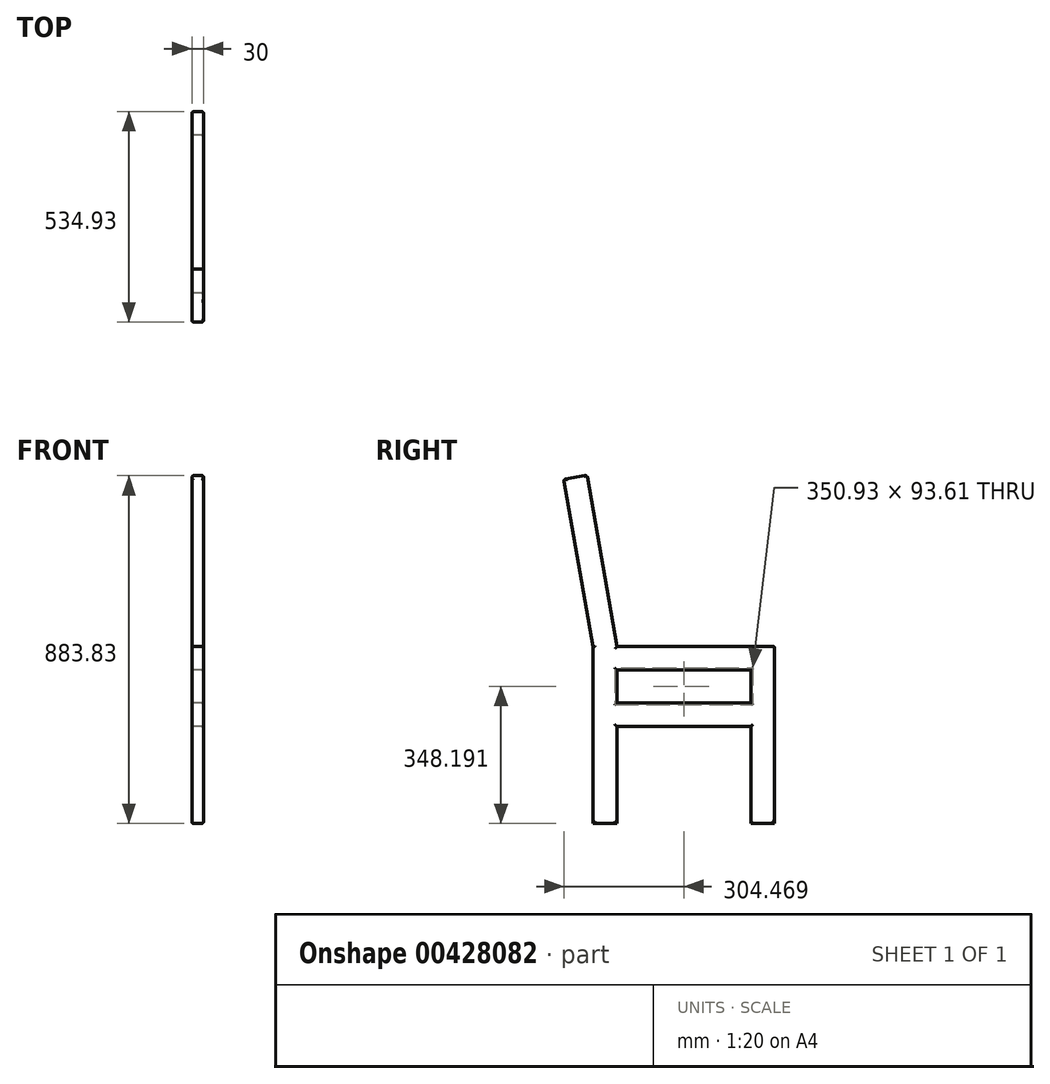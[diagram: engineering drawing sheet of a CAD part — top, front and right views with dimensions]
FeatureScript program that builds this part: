
annotation { "Feature Type Name" : "Feature", "Feature Type Description" : "" }
export const myFeature = defineFeature(function(context is Context, id is Id, definition is map)
    precondition{}
    {
        {
            var Q0;
            Q0=qCreatedBy(makeId("Right.planeOp"),FACE);
            var sketch = newSketch(context, id + "F0", { "sketchPlane" : qUnion([Q0])});
            skLineSegment(sketch, "E0", {"start": v(-254.48, -181.61) * mm, "end": v(-254.48, 268.39) * mm});
            skLineSegment(sketch, "E1", {"start": v(-254.48, 268.39) * mm, "end": v(-329.28, 692.6) * mm});
            skLineSegment(sketch, "E2", {"start": v(-329.28, 692.6) * mm, "end": v(-270.2, 703.02) * mm});
            skLineSegment(sketch, "E3", {"start": v(-270.2, 703.02) * mm, "end": v(-193.56, 268.39) * mm});
            skLineSegment(sketch, "E4", {"start": v(-193.56, 268.39) * mm, "end": v(206.44, 268.39) * mm});
            skLineSegment(sketch, "E5", {"start": v(206.44, 268.39) * mm, "end": v(206.44, -181.61) * mm});
            skLineSegment(sketch, "E6", {"start": v(206.44, -181.61) * mm, "end": v(146.44, -181.61) * mm});
            skLineSegment(sketch, "E7", {"start": v(146.44, -181.61) * mm, "end": v(146.44, 208.39) * mm});
            skLineSegment(sketch, "E8", {"start": v(146.44, 208.39) * mm, "end": v(-194.48, 208.39) * mm});
            skLineSegment(sketch, "E9", {"start": v(-194.48, 208.39) * mm, "end": v(-194.48, -181.61) * mm});
            skLineSegment(sketch, "E10", {"start": v(-194.48, -181.61) * mm, "end": v(-254.48, -181.61) * mm});
            skLineSegment(sketch, "E11", {"start": v(-194.48, 124.78) * mm, "end": v(146.44, 124.78) * mm});
            skLineSegment(sketch, "E12", {"start": v(-194.48, 64.78) * mm, "end": v(146.44, 64.78) * mm});
            skSolve(sketch);
        }
        {
            var Q0;
            Q0 = qSketchRegion(id + "F0", true);
            extrude(context, id + "F1", {"entities" : qUnion([Q0]), "depth" : 30 * mm});
        }
        {
            var Q0;
            Q0=makeQuery(id+"F1.opExtrude","CAP_FACE",FACE,{"disambiguationData":[OSD([sQuery(id+"F0.wireOp",EDGE,"E0"),sQuery(id+"F0.wireOp",EDGE,"E1"),sQuery(id+"F0.wireOp",EDGE,"E2"),sQuery(id+"F0.wireOp",EDGE,"E3"),sQuery(id+"F0.wireOp",EDGE,"E4"),sQuery(id+"F0.wireOp",EDGE,"E5"),sQuery(id+"F0.wireOp",EDGE,"E6"),sQuery(id+"F0.wireOp",EDGE,"E7"),sQuery(id+"F0.wireOp",EDGE,"E8"),sQuery(id+"F0.wireOp",EDGE,"E9"),sQuery(id+"F0.wireOp",EDGE,"E10")])],"isStart":false});
            var Q1;
            Q1=makeQuery(id+"F1.opExtrude","CAP_FACE",FACE,{"disambiguationData":[OSD([sQuery(id+"F0.wireOp",EDGE,"E0"),sQuery(id+"F0.wireOp",EDGE,"E1"),sQuery(id+"F0.wireOp",EDGE,"E2"),sQuery(id+"F0.wireOp",EDGE,"E3"),sQuery(id+"F0.wireOp",EDGE,"E4"),sQuery(id+"F0.wireOp",EDGE,"E5"),sQuery(id+"F0.wireOp",EDGE,"E6"),sQuery(id+"F0.wireOp",EDGE,"E7"),sQuery(id+"F0.wireOp",EDGE,"E8"),sQuery(id+"F0.wireOp",EDGE,"E9"),sQuery(id+"F0.wireOp",EDGE,"E10")])],"isStart":true});
            fillet(context, id + "F2", {"entities" : qUnion([Q0, Q1]), "radius" : 5 * mm, "tangentPropagation" : true, "allowEdgeOverflow" : false});
        }
        {
            var Q0;
            Q0=makeQuery(id+"F1.opExtrude","SWEPT_EDGE",EDGE,{"disambiguationData":[OSD([sQuery(id+"F0.wireOp",EDGE,"E4"),sQuery(id+"F0.wireOp",EDGE,"E5")])]});
            var Q1;
            Q1=makeQuery(id+"F1.opExtrude","SWEPT_EDGE",EDGE,{"disambiguationData":[OSD([sQuery(id+"F0.wireOp",EDGE,"E2"),sQuery(id+"F0.wireOp",EDGE,"E3")])]});
            var Q2;
            Q2=makeQuery(id+"F1.opExtrude","SWEPT_EDGE",EDGE,{"disambiguationData":[OSD([sQuery(id+"F0.wireOp",EDGE,"E1"),sQuery(id+"F0.wireOp",EDGE,"E2")])]});
            fillet(context, id + "F3", {"entities" : qUnion([Q0, Q1, Q2]), "radius" : 5 * mm, "tangentPropagation" : true, "allowEdgeOverflow" : false});
        }
    });
